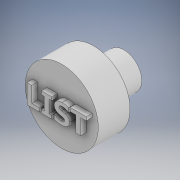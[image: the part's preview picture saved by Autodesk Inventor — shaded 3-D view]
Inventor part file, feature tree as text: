
AUTODESK INVENTOR PART (.ipt)
format: ipt  version: 2022 (Build 260153000, 153)  size: 185,856 bytes
history: native  units: in
note: dims shown in document units (in); Inventor stores cm internally (conversion verified against a paired STEP export)
features: sketch x3, extrude x3
ambient origin geometry x8: Origin, YZ Plane, XZ Plane, XY Plane, X Axis, Y Axis, Z Axis, Center Point
bodies: Solid1 (feature_tree)
feature tree (6):
  sketch  "Sketch1"  dims[d0=0.4898in d1=0.0185in]
  extrude  "Extrusion1"  Depth=0.0185in
  extrude  "Extrusion2"  Depth=0.189in TaperAngle=0.0deg
  sketch  "Sketch2"  dims[d2=0.1969in d3=0.0in d4=0.189in d5=0.0in]
  extrude  "Extrusion5"  [1 undecoded]
  sketch  "Sketch3"  dims[d10=0.0354in d11=0.0in]
note: 1 required parameter value undecoded (feature->parameter linkage not recoverable at this tier; creation-order binding heuristic only, values carry confidence <= 0.55)
